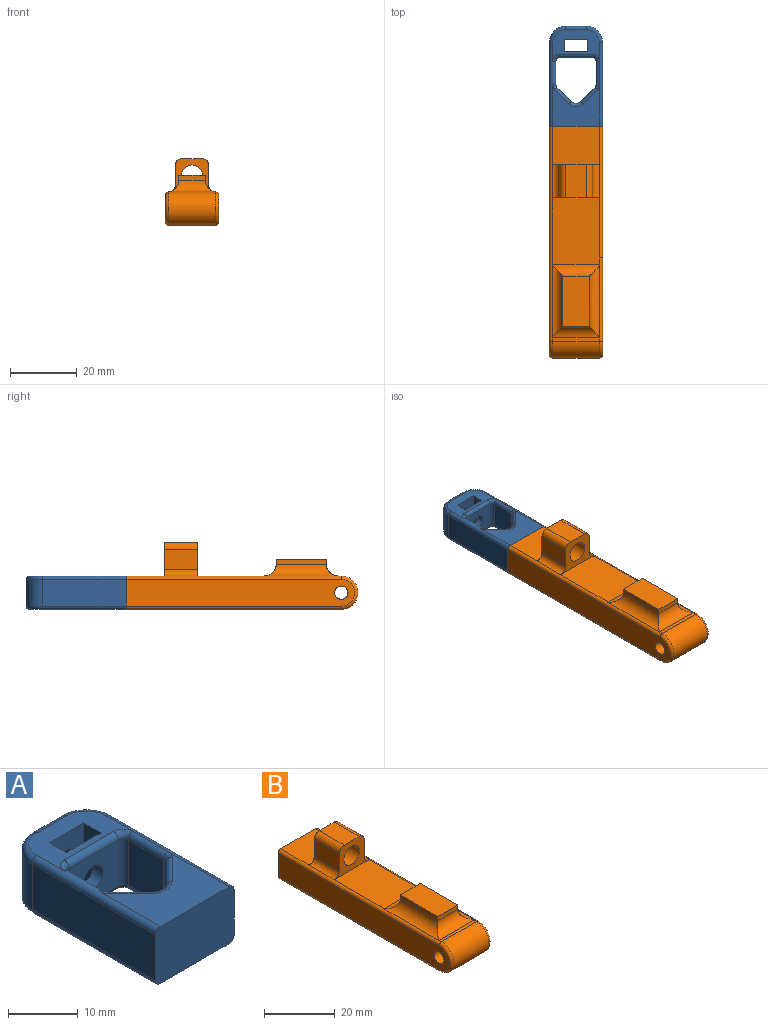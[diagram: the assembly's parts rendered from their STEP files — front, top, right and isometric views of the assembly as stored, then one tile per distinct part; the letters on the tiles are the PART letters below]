
ASSEMBLY  parts=2 mates=1
PART A: 54 faces, bbox 16.8x30.4x10 mm
  f0: plane 16x10mm, normal (0,-1,0), area 159.1mm2, adj f46,f47,f48,f49,f50,f51,f52,f53
  f1: cylinder r=2mm len=4mm, axis (0,1,0), area 50.3mm2, adj f9,f16
  f2: cylinder r=2mm len=4mm, axis (0,1,0), area 25.1mm2, adj f3,f18
  f3: plane 10x8mm, normal (0,-1,0), area 67.4mm2, adj f2,f4,f10,f12,f20
  f4: cylinder r=1mm len=8mm, axis (0,0,1), area 12.6mm2, adj f3,f13,f21,f22
  f5: cylinder r=1mm len=8mm, axis (0,0,1), area 6.3mm2, adj f6,f21,f26,f27
  f6: plane 8x4.29mm, normal (-0.71,0.71,0), area 48.6mm2, adj f5,f7,f25,f28
  f7: cylinder r=2mm len=8mm, axis (0,0,1), area 25.1mm2, adj f6,f8,f24,f29
  f8: plane 8x4.29mm, normal (0.71,0.71,0), area 48.6mm2, adj f7,f11,f23,f30
  f9: plane 8x6mm, normal (0,1,0), area 35.4mm2, adj f1,f14,f19,f31,f32
  f10: cylinder r=1mm len=8mm, axis (0,0,1), area 12.6mm2, adj f3,f34,f37,f38
  f11: cylinder r=1mm len=8mm, axis (0,0,1), area 6.3mm2, adj f8,f33,f38,f39
  f12: cylinder r=1mm len=10mm, axis (-1,0,0), area 15.7mm2, adj f3,f13,f37,f41
  f13: torus R=2mm, axis (0,0,1), area 3.4mm2, adj f4,f12,f40,f41
  f14: cylinder r=1mm len=6mm, axis (1,0,0), area 9.4mm2, adj f9,f36,f41,f42
  f15: plane 10x3.5mm, normal (1,0,0), area 35mm2, adj f16,f18,f41,f44
  f16: plane 10x7mm, normal (0,-1,0), area 57.4mm2, adj f1,f15,f17,f41,f44
  f17: plane 10x3.5mm, normal (-1,0,0), area 35mm2, adj f16,f18,f41,f44
  f18: plane 10x7mm, normal (0,1,0), area 57.4mm2, adj f2,f15,f17,f41,f44
  f19: cylinder r=1mm len=6mm, axis (-1,0,0), area 9.4mm2, adj f9,f35,f43,f44
  f20: cylinder r=1mm len=10mm, axis (1,0,0), area 15.7mm2, adj f3,f22,f34,f44
  f21: plane 8x7.09mm, normal (-1,0,0), area 56.7mm2, adj f4,f5,f40,f45
  f22: torus R=2mm, axis (0,0,1), area 3.4mm2, adj f4,f20,f44,f45
  f23: cylinder r=1mm len=5mm, axis (0.71,-0.71,0), area 9.5mm2, adj f8,f24,f39,f53
  f24: torus R=3mm, axis (0,0,1), area 5.8mm2, adj f7,f23,f25,f53
  f25: cylinder r=1mm len=5mm, axis (0.71,0.71,0), area 9.5mm2, adj f6,f24,f26,f53
  f26: torus R=2mm, axis (0,0,1), area 1.7mm2, adj f5,f25,f40,f53
  f27: torus R=2mm, axis (0,0,1), area 1.7mm2, adj f5,f28,f45,f52
  f28: cylinder r=1mm len=5mm, axis (-0.71,-0.71,0), area 9.5mm2, adj f6,f27,f29,f52
  f29: torus R=3mm, axis (0,0,1), area 5.8mm2, adj f7,f28,f30,f52
  f30: cylinder r=1mm len=5mm, axis (-0.71,0.71,0), area 9.5mm2, adj f8,f29,f33,f52
  f31: cylinder r=5mm len=8mm, axis (0,0,-1), area 62.8mm2, adj f9,f35,f36,f51
  f32: cylinder r=5mm len=8mm, axis (0,0,-1), area 62.8mm2, adj f9,f42,f43,f48
  f33: torus R=2mm, axis (0,0,1), area 1.7mm2, adj f11,f30,f50,f52
  f34: torus R=2mm, axis (0,0,1), area 3.4mm2, adj f10,f20,f44,f50
  f35: torus R=4mm, axis (0,0,1), area 11.4mm2, adj f19,f31,f44,f50
  f36: torus R=4mm, axis (0,0,1), area 11.4mm2, adj f14,f31,f41,f49
  f37: torus R=2mm, axis (0,0,1), area 3.4mm2, adj f10,f12,f41,f49
  f38: plane 8x7.09mm, normal (1,0,0), area 56.7mm2, adj f10,f11,f49,f50
  f39: torus R=2mm, axis (0,0,1), area 1.7mm2, adj f11,f23,f49,f53
  f40: cylinder r=1mm len=7.09mm, axis (0,1,0), area 11.1mm2, adj f13,f21,f26,f46
  f41: plane 14x9.5mm, normal (0,0,1), area 75.3mm2, adj f12,f13,f14,f15,f16,f17,f18,f36
  f42: torus R=4mm, axis (0,0,1), area 11.4mm2, adj f14,f32,f41,f46
  f43: torus R=4mm, axis (0,0,1), area 11.4mm2, adj f19,f32,f44,f47
  f44: plane 14x9.5mm, normal (0,0,-1), area 75.3mm2, adj f15,f16,f17,f18,f19,f20,f22,f34
  f45: cylinder r=1mm len=7.09mm, axis (0,-1,0), area 11.1mm2, adj f21,f22,f27,f47
  f46: cylinder r=1mm len=25mm, axis (0,-1,0), area 39.3mm2, adj f0,f40,f41,f42,f48,f53
  f47: cylinder r=1mm len=25mm, axis (0,1,0), area 39.3mm2, adj f0,f43,f44,f45,f48,f52
  f48: plane 25x8mm, normal (1,0,0), area 200mm2, adj f0,f32,f46,f47
  f49: cylinder r=1mm len=25mm, axis (0,-1,0), area 50.4mm2, adj f0,f36,f37,f38,f39,f41,f51,f53
  f50: cylinder r=1mm len=25mm, axis (0,1,0), area 50.4mm2, adj f0,f33,f34,f35,f38,f44,f51,f52
  f51: plane 25x8mm, normal (-1,0,0), area 200mm2, adj f0,f31,f49,f50
  f52: plane 14x12.41mm, normal (0,0,-1), area 115.3mm2, adj f0,f27,f28,f29,f30,f33,f47,f50
  f53: plane 14x12.41mm, normal (0,0,1), area 115.3mm2, adj f0,f23,f24,f25,f26,f39,f46,f49
PART B: 40 faces, bbox 16x76.5x20.4 mm
  f0: plane 14x11.51mm, normal (0,0,1), area 161.1mm2, adj f1,f15,f29,f30
  f1: cylinder r=1mm len=39.5mm, axis (0,-1,0), area 62mm2, adj f0,f4,f7,f18,f29,f37
  f2: cylinder r=1mm len=39.5mm, axis (0,-1,0), area 62mm2, adj f5,f7,f20,f29
  f3: plane 14x0.99mm, normal (0,0,1), area 13.9mm2, adj f15,f16,f18,f27
  f4: plane 20x14mm, normal (0,0,1), area 279.9mm2, adj f1,f15,f18,f22,f32
  f5: plane 64.49x14mm, normal (0,0,-1), area 902.9mm2, adj f2,f14,f16,f20,f29
  f6: plane 68.49x8mm, normal (-1,0,0), area 528.5mm2, adj f8,f14,f15,f17,f29
  f7: plane 68.49x8mm, normal (1,0,0), area 528.5mm2, adj f1,f2,f8,f18,f19,f20,f29
  f8: cylinder r=2mm len=16mm, axis (1,0,0), area 201.1mm2, adj f6,f7
  f9: plane 8x1.5mm, normal (0,-1,0), area 12mm2, adj f10,f12,f13,f27
  f10: plane 15x1.53mm, normal (1,0,0), area 22.9mm2, adj f9,f11,f13,f22,f26,f27
  f11: plane 8x1.5mm, normal (0,1,0), area 12mm2, adj f10,f12,f13,f22
  f12: plane 15x1.53mm, normal (-1,0,0), area 22.9mm2, adj f9,f11,f13,f22,f25,f27
  f13: plane 15x8mm, normal (0,0,1), area 120mm2, adj f9,f10,f11,f12
  f14: cylinder r=1mm len=64.49mm, axis (0,1,0), area 101.3mm2, adj f5,f6,f17,f29
  f15: cylinder r=1mm len=64.49mm, axis (0,-1,0), area 98.9mm2, adj f0,f3,f4,f6,f17,f21,f24,f25
  f16: cylinder r=5mm len=14mm, axis (-1,0,0), area 219.9mm2, adj f3,f5,f17,f19
  f17: torus R=4mm, axis (-1,0,0), area 22.9mm2, adj f6,f14,f15,f16
  f18: cylinder r=1mm len=24.99mm, axis (0,-1,0), area 36.8mm2, adj f1,f3,f4,f7,f19,f23,f26,f28
  f19: torus R=4mm, axis (-1,0,0), area 22.9mm2, adj f7,f16,f18,f20
  f20: cylinder r=1mm len=24.99mm, axis (0,1,0), area 39.3mm2, adj f2,f5,f7,f19
  f21: torus R=4.5mm, axis (0,1,0), area 0mm2, adj f15,f22,f25
  f22: cylinder r=3.5mm len=14mm, axis (1,0,0), area 57.3mm2, adj f4,f10,f11,f12,f21,f23,f25,f26
  f23: torus R=4.5mm, axis (0,1,0), area 0mm2, adj f18,f22,f26
  f24: torus R=4.5mm, axis (0,1,0), area 0mm2, adj f15,f25,f27
  f25: cylinder r=3.5mm len=22mm, axis (0,-1,0), area 88.5mm2, adj f12,f15,f21,f22,f24,f27
  f26: bspline ~57x3.48mm, area 88.5mm2, adj f10,f18,f22,f23,f27,f28
  f27: cylinder r=3.5mm len=14mm, axis (-1,0,0), area 57.3mm2, adj f3,f9,f10,f12,f24,f25,f26,f28
  f28: torus R=4.5mm, axis (0,1,0), area 0mm2, adj f18,f26,f27
  f29: plane 16x10mm, normal (0,1,0), area 159.1mm2, adj f0,f1,f2,f5,f6,f7,f14,f15
  f30: plane 14x10mm, normal (0,1,0), area 69.8mm2, adj f0,f31,f33,f34,f35,f36,f37,f38
  f31: plane 10x6mm, normal (-1,0,0), area 60mm2, adj f30,f32,f36,f38
  f32: plane 14x10mm, normal (0,-1,0), area 69.8mm2, adj f4,f31,f33,f34,f35,f36,f37,f38
  f33: plane 10x6mm, normal (1,0,0), area 60mm2, adj f30,f32,f37,f39
  f34: plane 10x6mm, normal (0,0,1), area 60mm2, adj f30,f32,f38,f39
  f35: cylinder r=3.1mm len=10mm, axis (0,1,0), area 194.8mm2, adj f30,f32
  f36: cylinder r=2mm len=10mm, axis (0,-1,0), area 31.4mm2, adj f15,f30,f31,f32
  f37: cylinder r=2mm len=10mm, axis (0,1,0), area 31.4mm2, adj f1,f30,f32,f33
  f38: cylinder r=2mm len=10mm, axis (0,1,0), area 31.4mm2, adj f30,f31,f32,f34
  f39: cylinder r=2mm len=10mm, axis (0,-1,0), area 31.4mm2, adj f30,f32,f33,f34
PLACE A t=(-9.02,-17.43,-1.78)mm
PLACE B t=(-9.02,-50.93,-1.78)mm fixed
MATE fastened B.f29 <-> A.f1  axis (0,1,0) through (-4.78,-24.56,6.36)mm
